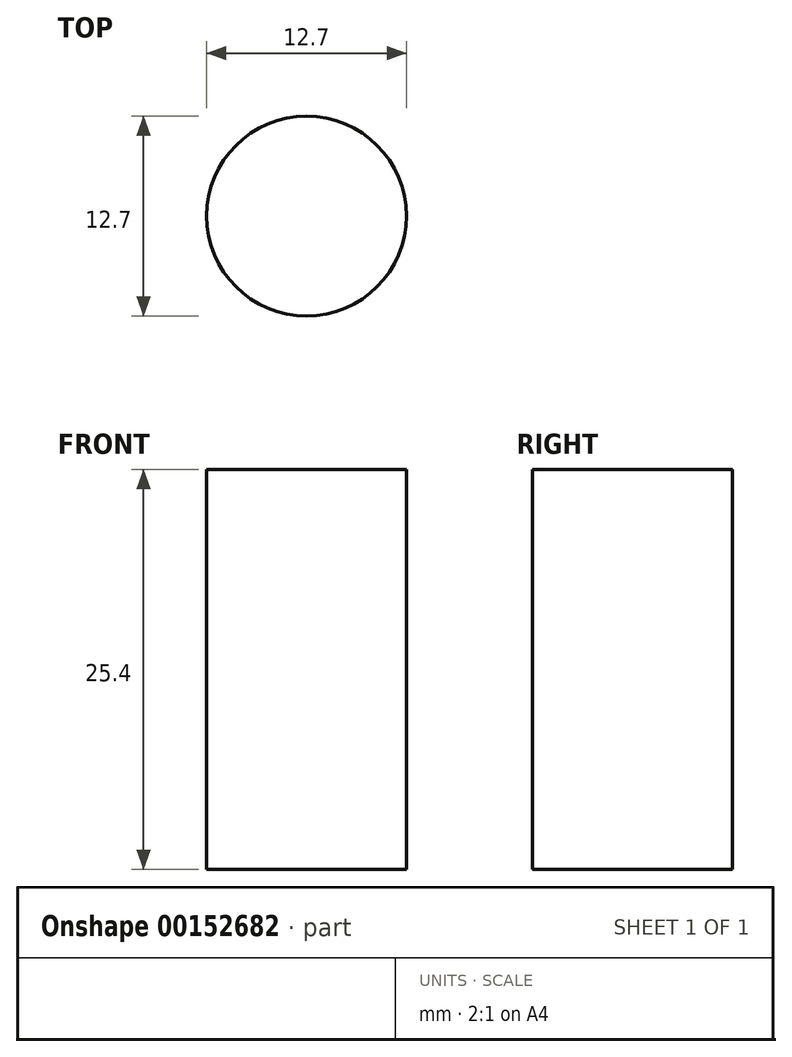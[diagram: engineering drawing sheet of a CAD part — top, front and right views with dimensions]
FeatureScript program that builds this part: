
annotation { "Feature Type Name" : "Feature", "Feature Type Description" : "" }
export const myFeature = defineFeature(function(context is Context, id is Id, definition is map)
    precondition{}
    {
        {
            var Q0;
            Q0=qCreatedBy(makeId("Top.planeOp"),FACE);
            var sketch = newSketch(context, id + "F0", { "sketchPlane" : qUnion([Q0])});
            skLineSegment(sketch, "E0", {"start": v(0, 0) * mm, "end": v(0, -12.7) * mm, "construction": true});
            skLineSegment(sketch, "E1", {"start": v(0, 0) * mm, "end": v(-26.94, 26.94) * mm, "construction": true});
            skLineSegment(sketch, "E2", {"start": v(-26.94, 26.94) * mm, "end": v(15.46, 119.27) * mm, "construction": true});
            skLineSegment(sketch, "E3", {"start": v(0, 0) * mm, "end": v(42.4, 92.33) * mm, "construction": true});
            skLineSegment(sketch, "E4", {"start": v(15.46, 119.27) * mm, "end": v(42.4, 92.33) * mm, "construction": true});
            skLineSegment(sketch, "E5", {"start": v(42.4, 92.33) * mm, "end": v(42.4, 130.43) * mm, "construction": true});
            skLineSegment(sketch, "E6", {"start": v(42.4, 130.43) * mm, "end": v(15.46, 119.27) * mm, "construction": true});
            skLineSegment(sketch, "E7", {"start": v(42.4, 92.33) * mm, "end": v(127, 148.6) * mm, "construction": true});
            skLineSegment(sketch, "E8", {"start": v(42.4, 130.43) * mm, "end": v(127, 186.7) * mm, "construction": true});
            skLineSegment(sketch, "E9", {"start": v(127, 186.7) * mm, "end": v(127, 148.6) * mm, "construction": true});
            skLineSegment(sketch, "E10", {"start": v(127, 167.64) * mm, "end": v(228.6, 167.64) * mm, "construction": true});
            skLineSegment(sketch, "E11", {"start": v(0, -12.7) * mm, "end": v(228.6, -12.7) * mm, "construction": true});
            skLineSegment(sketch, "E12", {"start": v(228.6, -12.7) * mm, "end": v(228.6, 167.64) * mm, "construction": true});
            skLineSegment(sketch, "E13", {"start": v(21.2, 46.17) * mm, "end": v(17.6, 47.82) * mm, "construction": true});
            skLineSegment(sketch, "E14", {"start": v(-5.74, 73.1) * mm, "end": v(-2.13, 71.45) * mm, "construction": true});
            skLineSegment(sketch, "E15", {"start": v(84.7, 120.46) * mm, "end": v(86.36, 124.07) * mm, "construction": true});
            skLineSegment(sketch, "E16", {"start": v(86.36, 124.07) * mm, "end": v(127, 151.1) * mm, "construction": true});
            skLineSegment(sketch, "E17", {"start": v(17.6, 47.82) * mm, "end": v(39.4, 95.32) * mm, "construction": true});
            skLineSegment(sketch, "E18", {"start": v(84.7, 158.56) * mm, "end": v(86.9, 155.26) * mm, "construction": true});
            skCircle(sketch, "E19", {"center": v(228.6, -12.7) * mm, "radius": 6.35 * mm});
            skSolve(sketch);
        }
        {
            var Q0;
            Q0 = qSketchRegion(id + "F0", true);
            extrude(context, id + "F1", {"entities" : qUnion([Q0]), "depth" : 25.4 * mm});
        }
    });
